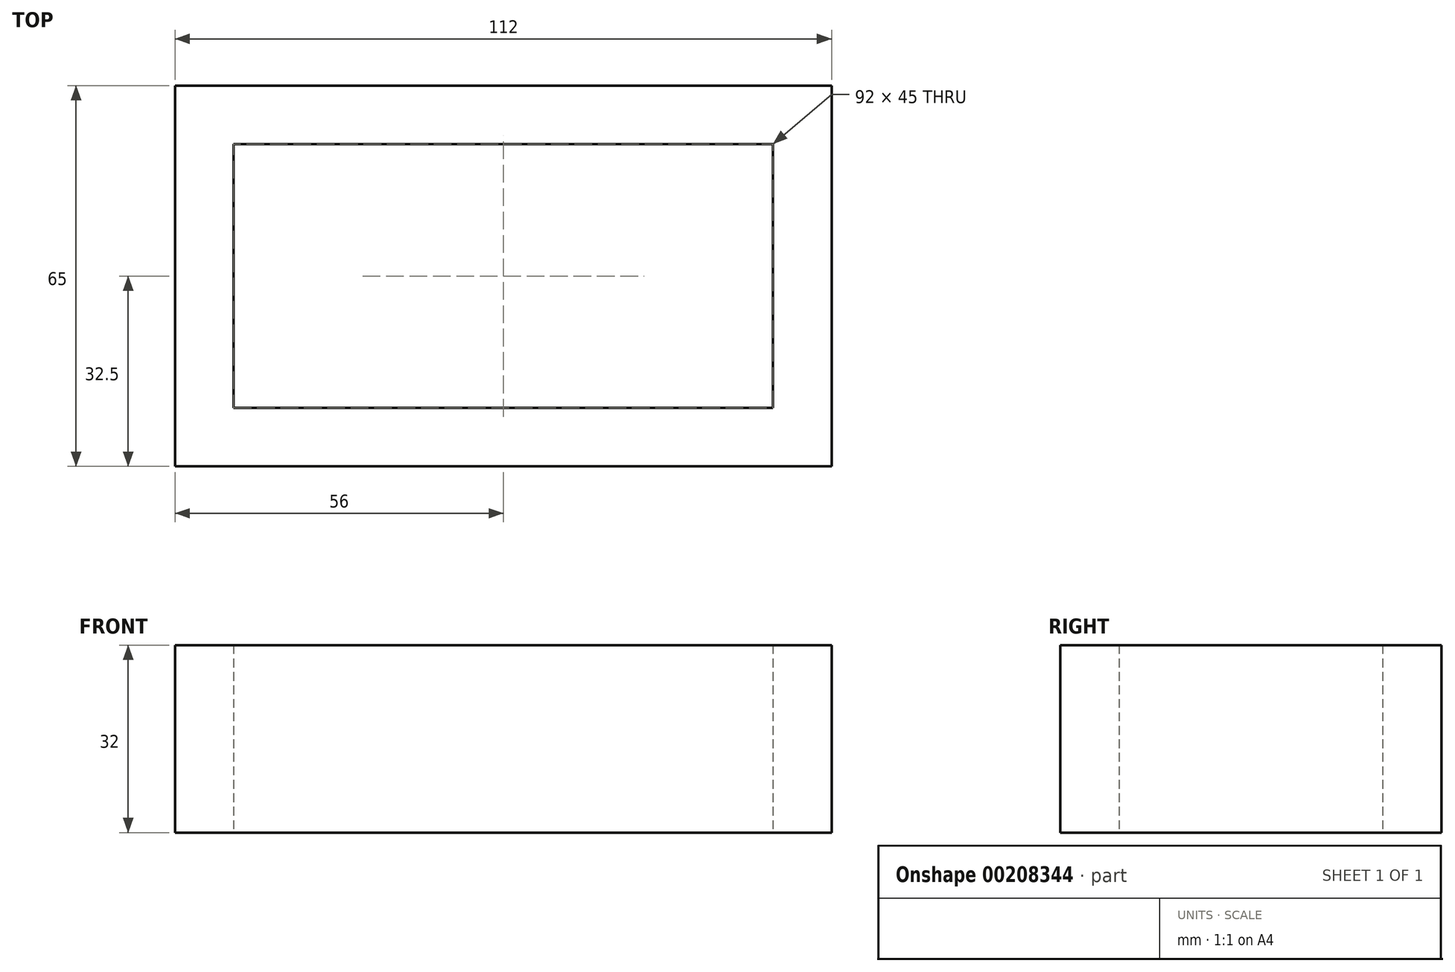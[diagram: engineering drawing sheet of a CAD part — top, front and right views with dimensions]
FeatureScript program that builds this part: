
annotation { "Feature Type Name" : "Feature", "Feature Type Description" : "" }
export const myFeature = defineFeature(function(context is Context, id is Id, definition is map)
    precondition{}
    {
        {
            var Q0;
            Q0=qCreatedBy(makeId("Top.planeOp"),FACE);
            var sketch = newSketch(context, id + "F0", { "sketchPlane" : qUnion([Q0])});
            skLineSegment(sketch, "E0.bottom", {"start": v(46, -22.5) * mm, "end": v(-46, -22.5) * mm});
            skLineSegment(sketch, "E0.top", {"start": v(46, 22.5) * mm, "end": v(-46, 22.5) * mm});
            skLineSegment(sketch, "E0.left", {"start": v(46, -22.5) * mm, "end": v(46, 22.5) * mm});
            skLineSegment(sketch, "E0.right", {"start": v(-46, -22.5) * mm, "end": v(-46, 22.5) * mm});
            skPoint(sketch, "E0.middle", {"position": v(0, 0) * mm});
            skLineSegment(sketch, "E1.bottom", {"start": v(56, -32.5) * mm, "end": v(-56, -32.5) * mm});
            skLineSegment(sketch, "E1.top", {"start": v(56, 32.5) * mm, "end": v(-56, 32.5) * mm});
            skLineSegment(sketch, "E1.left", {"start": v(56, -32.5) * mm, "end": v(56, 32.5) * mm});
            skLineSegment(sketch, "E1.right", {"start": v(-56, -32.5) * mm, "end": v(-56, 32.5) * mm});
            skSolve(sketch);
        }
        {
            var Q0;
            Q0=makeQuery(id+"F0.imprint","IMPRINT",FACE,{"disambiguationData":[TD([[makeQuery(id+"F0.imprint","IMPRINT",EDGE,{"derivedFrom":sQuery(id+"F0.wireOp",EDGE,"E0.bottom")}),1.0]])]});
            extrude(context, id + "F1", {"entities" : qUnion([Q0]), "depth" : 32 * mm});
        }
    });
